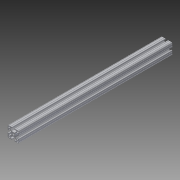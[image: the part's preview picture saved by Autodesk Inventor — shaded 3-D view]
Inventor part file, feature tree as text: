
AUTODESK INVENTOR PART (.ipt)
format: ipt  version: 2013 (Build 170138000, 138)  size: 289,792 bytes
history: native  units: in
note: dims shown in document units (in); Inventor stores cm internally (conversion verified against a paired STEP export)
features: extrude x1, sketch x1
ambient origin geometry x8: Origin, YZ Plane, XZ Plane, XY Plane, X Axis, Y Axis, Z Axis, Center Point
bodies: Solid1 (feature_tree)
feature tree (2):
  extrude  "Extrusion1"  [1 undecoded]
  sketch  "Sketch1"  dims[d0=20.75in d1=0.0in]
note: 1 required parameter value undecoded (feature->parameter linkage not recoverable at this tier; creation-order binding heuristic only, values carry confidence <= 0.55)
